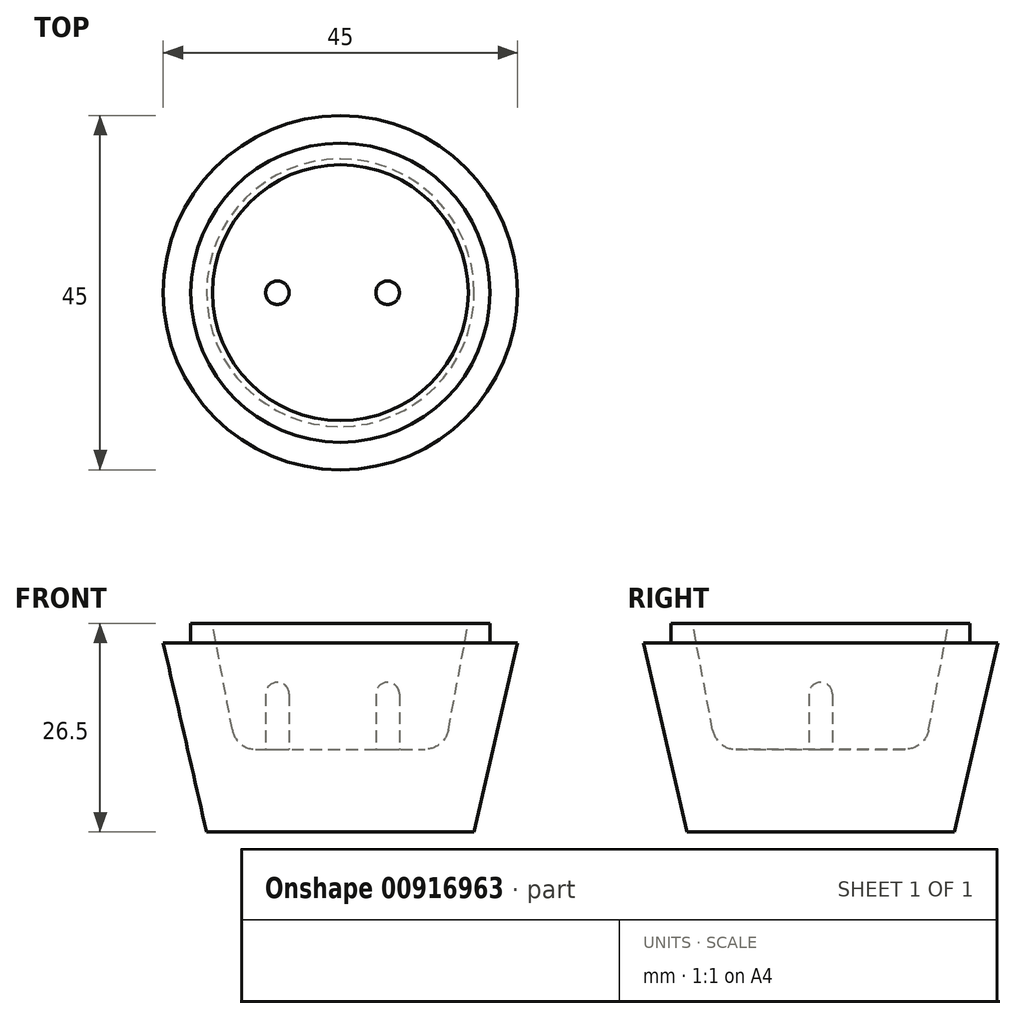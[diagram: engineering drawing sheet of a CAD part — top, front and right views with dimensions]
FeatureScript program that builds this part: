
annotation { "Feature Type Name" : "Feature", "Feature Type Description" : "" }
export const myFeature = defineFeature(function(context is Context, id is Id, definition is map)
    precondition{}
    {
        {
            var Q0;
            Q0=qCreatedBy(makeId("Front.planeOp"),FACE);
            var sketch = newSketch(context, id + "F0", { "sketchPlane" : qUnion([Q0])});
            skLineSegment(sketch, "E0", {"start": v(0, 0) * mm, "end": v(17, 0) * mm});
            skLineSegment(sketch, "E1", {"start": v(0, 0) * mm, "end": v(0, 24) * mm});
            skLineSegment(sketch, "E2", {"start": v(0, 24) * mm, "end": v(22.5, 24) * mm});
            skLineSegment(sketch, "E3", {"start": v(22.5, 24) * mm, "end": v(17, 0) * mm});
            skSolve(sketch);
        }
        {
            var Q0;
            Q0=makeQuery(id+"F0.imprint","IMPRINT",FACE,{"disambiguationData":[TD([[makeQuery(id+"F0.imprint","IMPRINT",EDGE,{"derivedFrom":sQuery(id+"F0.wireOp",EDGE,"E0")}),1.0]])]});
            var Q1;
            Q1=sQuery(id+"F0.wireOp",EDGE,"E1");
            revolve(context, id + "F1", {"surfaceOperationType" : NewSurfaceOperationType.NEW, "entities" : qUnion([Q0]), "axis" : qUnion([Q1]), "revolveType" : RevolveType.FULL});
        }
        {
            var Q0;
            Q0=makeQuery(id+"F1.opRevolve","SWEPT_FACE",FACE,{"disambiguationData":[OSD([sQuery(id+"F0.wireOp",EDGE,"E2")])]});
            var sketch = newSketch(context, id + "F2", { "sketchPlane" : qUnion([Q0])});
            skCircle(sketch, "E4", {"center": v(0, 0) * mm, "radius": 19 * mm});
            skSolve(sketch);
        }
        {
            var Q0;
            Q0=makeQuery(id+"F2.imprint","IMPRINT",FACE,{"disambiguationData":[TD([[makeQuery(id+"F2.imprint","IMPRINT",EDGE,{"derivedFrom":sQuery(id+"F2.wireOp",EDGE,"E4")}),1.0]])]});
            extrude(context, id + "F3", {"entities" : qUnion([Q0]), "operationType" : NewBodyOperationType.ADD, "depth" : 2.5 * mm, "offsetDistance" : 25 * mm});
        }
        {
            var Q0;
            Q0=qCreatedBy(makeId("Front.planeOp"),FACE);
            var sketch = newSketch(context, id + "F4", { "sketchPlane" : qUnion([Q0])});
            skLineSegment(sketch, "E5", {"start": v(0, 26.5) * mm, "end": v(0, 10.5) * mm});
            skLineSegment(sketch, "E6", {"start": v(0, 10.5) * mm, "end": v(13.25, 10.5) * mm});
            skLineSegment(sketch, "E7", {"start": v(0, 26.5) * mm, "end": v(16.25, 26.5) * mm});
            skLineSegment(sketch, "E8", {"start": v(16.25, 26.5) * mm, "end": v(13.25, 10.5) * mm});
            skSolve(sketch);
        }
        {
            var Q0;
            Q0 = qSketchRegion(id + "F4", true);
            var Q1;
            Q1=sQuery(id+"F4.wireOp",EDGE,"E5");
            revolve(context, id + "F5", {"operationType" : NewBodyOperationType.REMOVE, "surfaceOperationType" : NewSurfaceOperationType.NEW, "entities" : qUnion([Q0]), "axis" : qUnion([Q1]), "revolveType" : RevolveType.FULL, "oppositeDirection" : true});
        }
        {
            var Q0;
            Q0=makeQuery(id+"F5.boolean.opBoolean","COPY",EDGE,{"derivedFrom":makeQuery(id+"F5.opRevolve","SWEPT_EDGE",EDGE,{"disambiguationData":[OSD([sQuery(id+"F4.wireOp",EDGE,"E6"),sQuery(id+"F4.wireOp",EDGE,"E8")])]})});
            fillet(context, id + "F6", {"entities" : qUnion([Q0]), "radius" : 3 * mm, "tangentPropagation" : true, "allowEdgeOverflow" : false});
        }
        {
            var Q0;
            Q0=makeQuery(id+"F5.boolean.opBoolean","COPY",FACE,{"derivedFrom":makeQuery(id+"F5.opRevolve","SWEPT_FACE",FACE,{"disambiguationData":[OSD([sQuery(id+"F4.wireOp",EDGE,"E6")])]})});
            var sketch = newSketch(context, id + "F7", { "sketchPlane" : qUnion([Q0])});
            skCircle(sketch, "E9", {"center": v(-8, 0) * mm, "radius": 1.5 * mm});
            skCircle(sketch, "E10", {"center": v(6, 0) * mm, "radius": 1.5 * mm});
            skSolve(sketch);
        }
        {
            var Q0;
            Q0=makeQuery(id+"F7.imprint","IMPRINT",FACE,{"disambiguationData":[TD([[makeQuery(id+"F7.imprint","IMPRINT",EDGE,{"derivedFrom":sQuery(id+"F7.wireOp",EDGE,"E9")}),1.0]])]});
            var Q1;
            Q1=makeQuery(id+"F7.imprint","IMPRINT",FACE,{"disambiguationData":[TD([[makeQuery(id+"F7.imprint","IMPRINT",EDGE,{"derivedFrom":sQuery(id+"F7.wireOp",EDGE,"E10")}),1.0]])]});
            extrude(context, id + "F8", {"entities" : qUnion([Q0, Q1]), "operationType" : NewBodyOperationType.ADD, "depth" : 8.5 * mm, "offsetDistance" : 25 * mm});
        }
        {
            var Q0;
            Q0=makeQuery(id+"F8.opExtrude","CAP_EDGE",EDGE,{"disambiguationData":[OSD([sQuery(id+"F7.wireOp",EDGE,"E9")])],"isStart":false});
            var Q1;
            Q1=makeQuery(id+"F8.opExtrude","CAP_EDGE",EDGE,{"disambiguationData":[OSD([sQuery(id+"F7.wireOp",EDGE,"E10")])],"isStart":false});
            fillet(context, id + "F9", {"entities" : qUnion([Q0, Q1]), "radius" : 1.5 * mm, "tangentPropagation" : true, "allowEdgeOverflow" : false});
        }
    });
